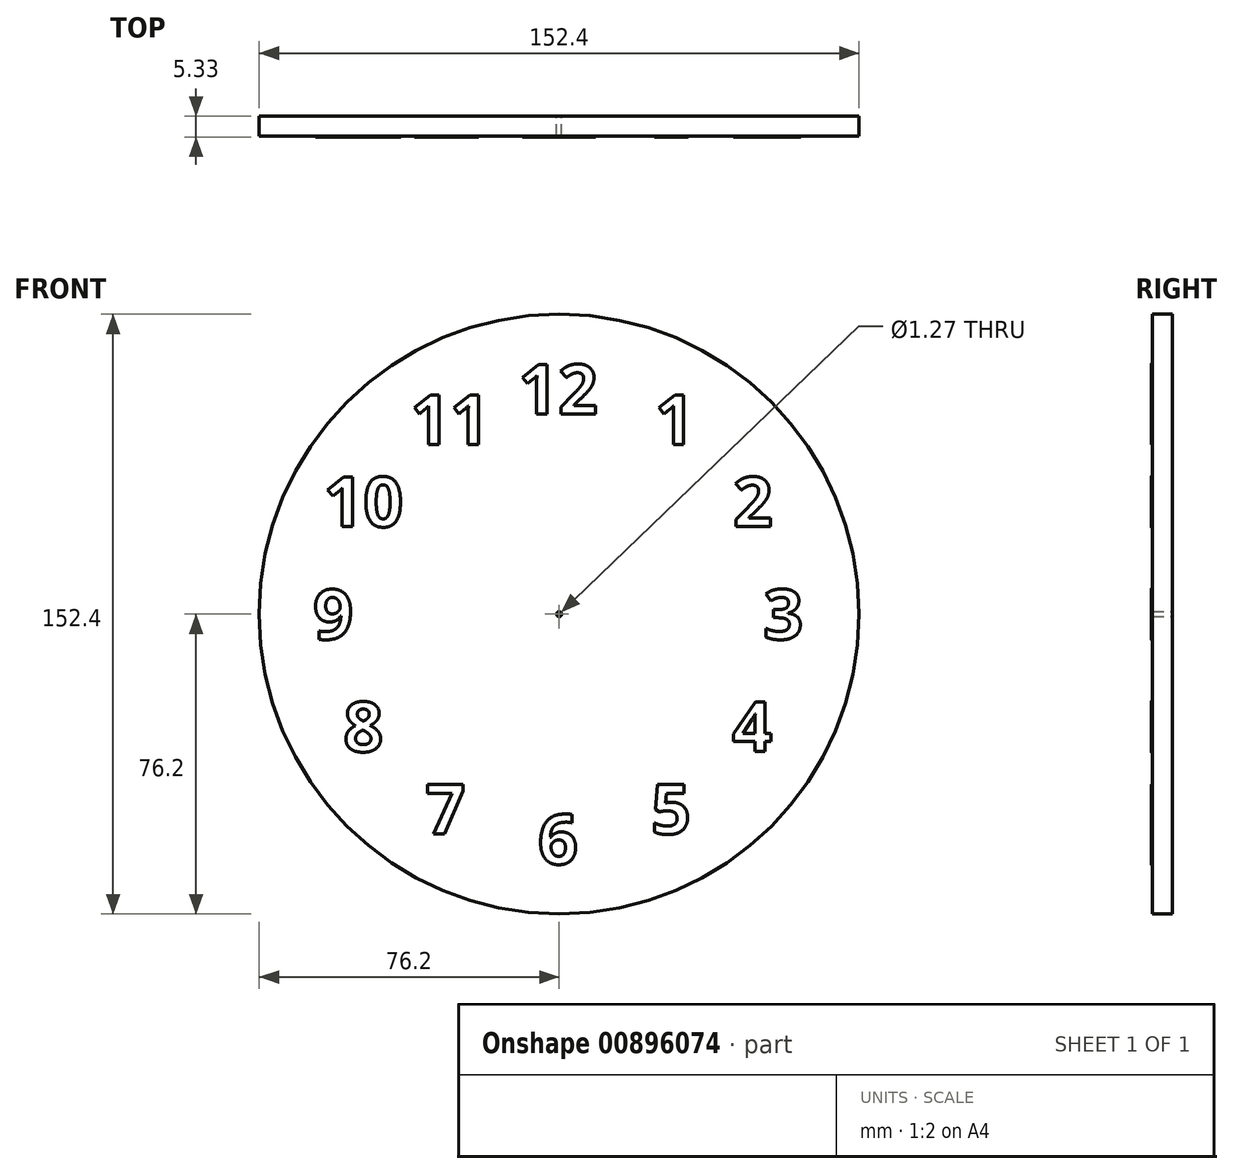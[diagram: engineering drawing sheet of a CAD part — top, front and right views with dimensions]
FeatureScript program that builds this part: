
annotation { "Feature Type Name" : "Feature", "Feature Type Description" : "" }
export const myFeature = defineFeature(function(context is Context, id is Id, definition is map)
    precondition{}
    {
        {
            var Q0;
            Q0=qCreatedBy(makeId("Front.planeOp"),FACE);
            var sketch = newSketch(context, id + "F0", { "sketchPlane" : qUnion([Q0])});
            skCircle(sketch, "E0", {"center": v(0, 0) * mm, "radius": 76.2 * mm});
            skCircle(sketch, "E1", {"center": v(0, 0) * mm, "radius": 0.64 * mm});
            skSolve(sketch);
        }
        {
            var Q0;
            Q0=makeQuery(id+"F0.imprint","IMPRINT",FACE,{"disambiguationData":[TD([[makeQuery(id+"F0.imprint","IMPRINT",EDGE,{"derivedFrom":sQuery(id+"F0.wireOp",EDGE,"E0")}),1.0]])]});
            extrude(context, id + "F1", {"entities" : qUnion([Q0]), "depth" : 5.08 * mm, "offsetDistance" : 25.4 * mm});
        }
        {
            var Q0;
            Q0=makeQuery(id+"F1.opExtrude","CAP_FACE",FACE,{"disambiguationData":[OSD([sQuery(id+"F0.wireOp",EDGE,"E0"),sQuery(id+"F0.wireOp",EDGE,"E1")])],"isStart":false});
            var sketch = newSketch(context, id + "F2", { "sketchPlane" : qUnion([Q0])});
            skPoint(sketch, "E2", {"position": v(0, 57.15) * mm});
            skPoint(sketch, "E3.1.0", {"position": v(-28.57, 49.5) * mm});
            skPoint(sketch, "E3.2.0", {"position": v(-49.5, 28.58) * mm});
            skPoint(sketch, "E3.3.0", {"position": v(-57.15, 0) * mm});
            skPoint(sketch, "E3.4.0", {"position": v(-49.5, -28.57) * mm});
            skPoint(sketch, "E3.5.0", {"position": v(-28.57, -49.5) * mm});
            skPoint(sketch, "E3.6.0", {"position": v(0, -57.15) * mm});
            skPoint(sketch, "E3.7.0", {"position": v(28.57, -49.5) * mm});
            skPoint(sketch, "E3.8.0", {"position": v(49.5, -28.58) * mm});
            skPoint(sketch, "E3.9.0", {"position": v(57.15, 0) * mm});
            skPoint(sketch, "E3.10.0", {"position": v(49.5, 28.58) * mm});
            skPoint(sketch, "E3.11.0", {"position": v(28.58, 49.5) * mm});
            skPoint(sketch, "E3.center", {"position": v(0, 0) * mm});
            skSolve(sketch);
        }
        {
            var Q0;
            Q0=makeQuery(id+"F2.imprint","IMPRINT",FACE,{"disambiguationData":[TD([[makeQuery(id+"F2.imprint","IMPRINT",EDGE,{"derivedFrom":makeQuery(id+"F1.opExtrude","CAP_EDGE",EDGE,{"disambiguationData":[OSD([sQuery(id+"F0.wireOp",EDGE,"E0")])],"isStart":false})}),1.0]])]});
            var sketch = newSketch(context, id + "F3", { "sketchPlane" : qUnion([Q0])});
            skText(sketch, "E4", { "text": "1", "fontName": "OpenSans-Bold.ttf"});
            skText(sketch, "E5", { "text": "2", "fontName": "OpenSans-Bold.ttf"});
            skText(sketch, "E6", { "text": "3", "fontName": "OpenSans-Bold.ttf"});
            skText(sketch, "E7", { "text": "4", "fontName": "OpenSans-Bold.ttf"});
            skText(sketch, "E8", { "text": "5", "fontName": "OpenSans-Bold.ttf"});
            skText(sketch, "E9", { "text": "6", "fontName": "OpenSans-Bold.ttf"});
            skText(sketch, "E10", { "text": "7", "fontName": "OpenSans-Bold.ttf"});
            skText(sketch, "E11", { "text": "8", "fontName": "OpenSans-Bold.ttf"});
            skText(sketch, "E12", { "text": "9", "fontName": "OpenSans-Bold.ttf"});
            skText(sketch, "E13", { "text": "10", "fontName": "OpenSans-Bold.ttf"});
            skText(sketch, "E14", { "text": "11", "fontName": "OpenSans-Bold.ttf"});
            skText(sketch, "E15", { "text": "12", "fontName": "OpenSans-Bold.ttf"});
            skPoint(sketch, "E16", {"position": v(-28.57, 49.5) * mm});
            skPoint(sketch, "E17", {"position": v(0, 57.15) * mm});
            skPoint(sketch, "E18", {"position": v(49.5, -28.58) * mm});
            skPoint(sketch, "E19", {"position": v(49.5, 28.58) * mm});
            skPoint(sketch, "E20", {"position": v(-49.5, -28.57) * mm});
            skPoint(sketch, "E21", {"position": v(57.15, 0) * mm});
            skPoint(sketch, "E22", {"position": v(28.58, 49.5) * mm});
            skPoint(sketch, "E23", {"position": v(28.57, -49.5) * mm});
            skPoint(sketch, "E24", {"position": v(0, -57.15) * mm});
            skPoint(sketch, "E25", {"position": v(-57.15, 0) * mm});
            skPoint(sketch, "E26", {"position": v(-28.57, -49.5) * mm});
            skPoint(sketch, "E27", {"position": v(-49.5, 28.58) * mm});
            const initialGuessF3  = {"E4": [0.02436, 0.04314, 1, 0, 0.0127], "E5": [0.04417, 0.02223, 1, 0, 0.0127], "E6": [0.05188, -0.00635, 1, 0, 0.0127], "E7": [0.04403, -0.03493, 1, 0, 0.0127], "E8": [0.02336, -0.05584, 1, 0, 0.0127], "E9": [-0.00533, -0.0635, 1, 0, 0.0127], "E10": [-0.0339, -0.05584, 1, 0, 0.0127], "E11": [-0.0548, -0.03492, 1, 0, 0.0127], "E12": [-0.06245, -0.00635, 1, 0, 0.0127], "E13": [-0.05982, 0.02223, 1, 0, 0.0127], "E14": [-0.03782, 0.04314, 1, 0, 0.0127], "E15": [-0.01036, 0.0508, 1, 0, 0.0127]};
            skSetInitialGuess(sketch, initialGuessF3);
            skSolve(sketch);
        }
        {
            var Q0;
            Q0 = qSketchRegion(id + "F3", true);
            extrude(context, id + "F4", {"entities" : qUnion([Q0]), "operationType" : NewBodyOperationType.ADD, "depth" : 0.25 * mm, "offsetDistance" : 25.4 * mm});
        }
    });
